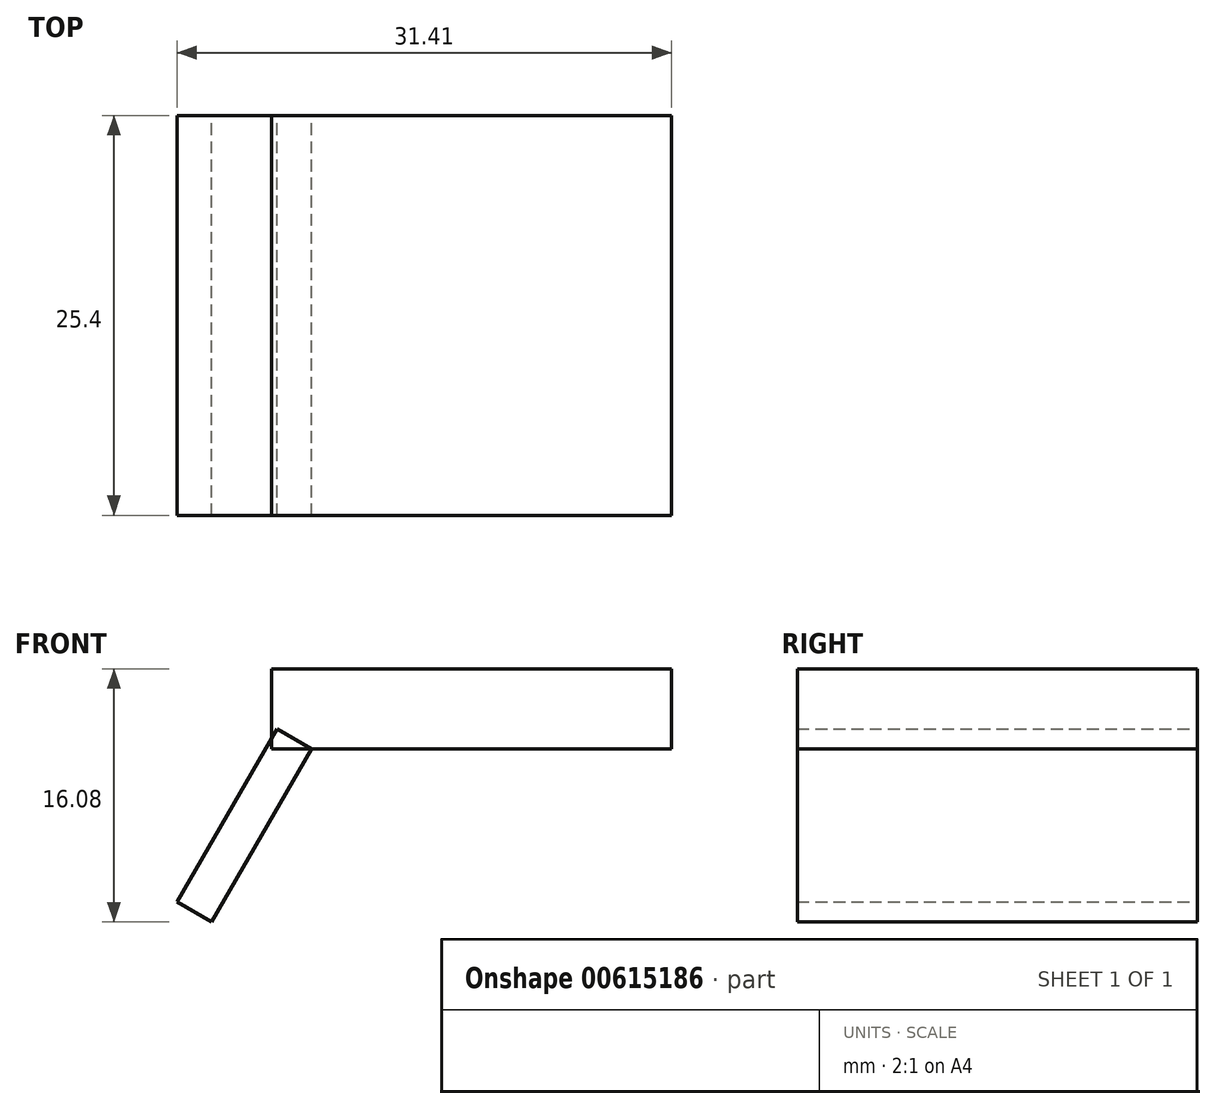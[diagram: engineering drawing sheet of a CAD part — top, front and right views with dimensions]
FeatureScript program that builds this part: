
annotation { "Feature Type Name" : "Feature", "Feature Type Description" : "" }
export const myFeature = defineFeature(function(context is Context, id is Id, definition is map)
    precondition{}
    {
        {
            var Q0;
            Q0=qCreatedBy(makeId("Top.planeOp"),FACE);
            var sketch = newSketch(context, id + "F0", { "sketchPlane" : qUnion([Q0])});
            skLineSegment(sketch, "E0.bottom", {"start": v(0, 0) * mm, "end": v(25.4, 0) * mm});
            skLineSegment(sketch, "E0.top", {"start": v(0, 25.4) * mm, "end": v(25.4, 25.4) * mm});
            skLineSegment(sketch, "E0.left", {"start": v(0, 0) * mm, "end": v(0, 25.4) * mm});
            skLineSegment(sketch, "E0.right", {"start": v(25.4, 0) * mm, "end": v(25.4, 25.4) * mm});
            skSolve(sketch);
        }
        {
            var Q0;
            Q0 = qSketchRegion(id + "F0", true);
            extrude(context, id + "F1", {"entities" : qUnion([Q0]), "depth" : 5.08 * mm, "offsetDistance" : 25.4 * mm});
        }
        {
            var Q0;
            Q0=qCreatedBy(makeId("Right.planeOp"),FACE);
            var sketch = newSketch(context, id + "F2", { "sketchPlane" : qUnion([Q0])});
            skLineSegment(sketch, "E1.bottom", {"start": v(0, 0) * mm, "end": v(25.4, 0) * mm});
            skLineSegment(sketch, "E1.top", {"start": v(0, -12.7) * mm, "end": v(25.4, -12.7) * mm});
            skLineSegment(sketch, "E1.left", {"start": v(0, 0) * mm, "end": v(0, -12.7) * mm});
            skLineSegment(sketch, "E1.right", {"start": v(25.4, 0) * mm, "end": v(25.4, -12.7) * mm});
            skSolve(sketch);
        }
        {
            var Q0;
            Q0=makeQuery(id+"F2.imprint","IMPRINT",FACE,{"disambiguationData":[TD([[makeQuery(id+"F2.imprint","IMPRINT",EDGE,{"derivedFrom":sQuery(id+"F2.wireOp",EDGE,"E1.bottom")}),-1.0]])]});
            extrude(context, id + "F3", {"entities" : qUnion([Q0]), "depth" : 2.54 * mm, "offsetDistance" : 25.4 * mm});
        }
        {
            var Q0;
            Q0=makeQuery(id+"F3.opExtrude","SWEPT_BODY",BODY,{"disambiguationData":[OSD([sQuery(id+"F2.wireOp",EDGE,"E1.bottom"),sQuery(id+"F2.wireOp",EDGE,"E1.top"),sQuery(id+"F2.wireOp",EDGE,"E1.left"),sQuery(id+"F2.wireOp",EDGE,"E1.right")])]});
            var Q1;
            Q1=makeQuery(id+"F3.opExtrude","CAP_EDGE",EDGE,{"disambiguationData":[OSD([sQuery(id+"F2.wireOp",EDGE,"E1.bottom")])],"isStart":false});
            transform(context, id + "F4", {"entities" : qUnion([Q0]), "transformType" : TransformType.ROTATION, "transformAxis" : qUnion([Q1]), "angle" : 30 * degree, "makeCopy" : false});
        }
        {
            var Q0;
            Q0=makeQuery(id+"F3.opExtrude","SWEPT_BODY",BODY,{"disambiguationData":[OSD([sQuery(id+"F2.wireOp",EDGE,"E1.bottom"),sQuery(id+"F2.wireOp",EDGE,"E1.top"),sQuery(id+"F2.wireOp",EDGE,"E1.left"),sQuery(id+"F2.wireOp",EDGE,"E1.right")])]});
            transform(context, id + "F5", {"entities" : qUnion([Q0]), "transformType" : TransformType.COPY});
        }
        {
            var Q0;
            Q0=makeQuery(id+"F3.opExtrude","SWEPT_BODY",BODY,{"disambiguationData":[OSD([sQuery(id+"F2.wireOp",EDGE,"E1.bottom"),sQuery(id+"F2.wireOp",EDGE,"E1.top"),sQuery(id+"F2.wireOp",EDGE,"E1.left"),sQuery(id+"F2.wireOp",EDGE,"E1.right")])]});
            transform(context, id + "F6", {"entities" : qUnion([Q0]), "transformType" : TransformType.COPY});
        }
        {
            var Q0;
            Q0=makeQuery(id+"F3.opExtrude","SWEPT_BODY",BODY,{"disambiguationData":[OSD([sQuery(id+"F2.wireOp",EDGE,"E1.bottom"),sQuery(id+"F2.wireOp",EDGE,"E1.top"),sQuery(id+"F2.wireOp",EDGE,"E1.left"),sQuery(id+"F2.wireOp",EDGE,"E1.right")])]});
            transform(context, id + "F7", {"entities" : qUnion([Q0]), "transformType" : TransformType.COPY});
        }
        {
            var Q0;
            Q0=makeQuery(id+"F3.opExtrude","SWEPT_BODY",BODY,{"disambiguationData":[OSD([sQuery(id+"F2.wireOp",EDGE,"E1.bottom"),sQuery(id+"F2.wireOp",EDGE,"E1.top"),sQuery(id+"F2.wireOp",EDGE,"E1.left"),sQuery(id+"F2.wireOp",EDGE,"E1.right")])]});
            transform(context, id + "F8", {"entities" : qUnion([Q0]), "transformType" : TransformType.COPY});
        }
        {
            var Q0;
            Q0=makeQuery(id+"F3.opExtrude","SWEPT_BODY",BODY,{"disambiguationData":[OSD([sQuery(id+"F2.wireOp",EDGE,"E1.bottom"),sQuery(id+"F2.wireOp",EDGE,"E1.top"),sQuery(id+"F2.wireOp",EDGE,"E1.left"),sQuery(id+"F2.wireOp",EDGE,"E1.right")])]});
            transform(context, id + "F9", {"entities" : qUnion([Q0]), "transformType" : TransformType.COPY});
        }
    });
